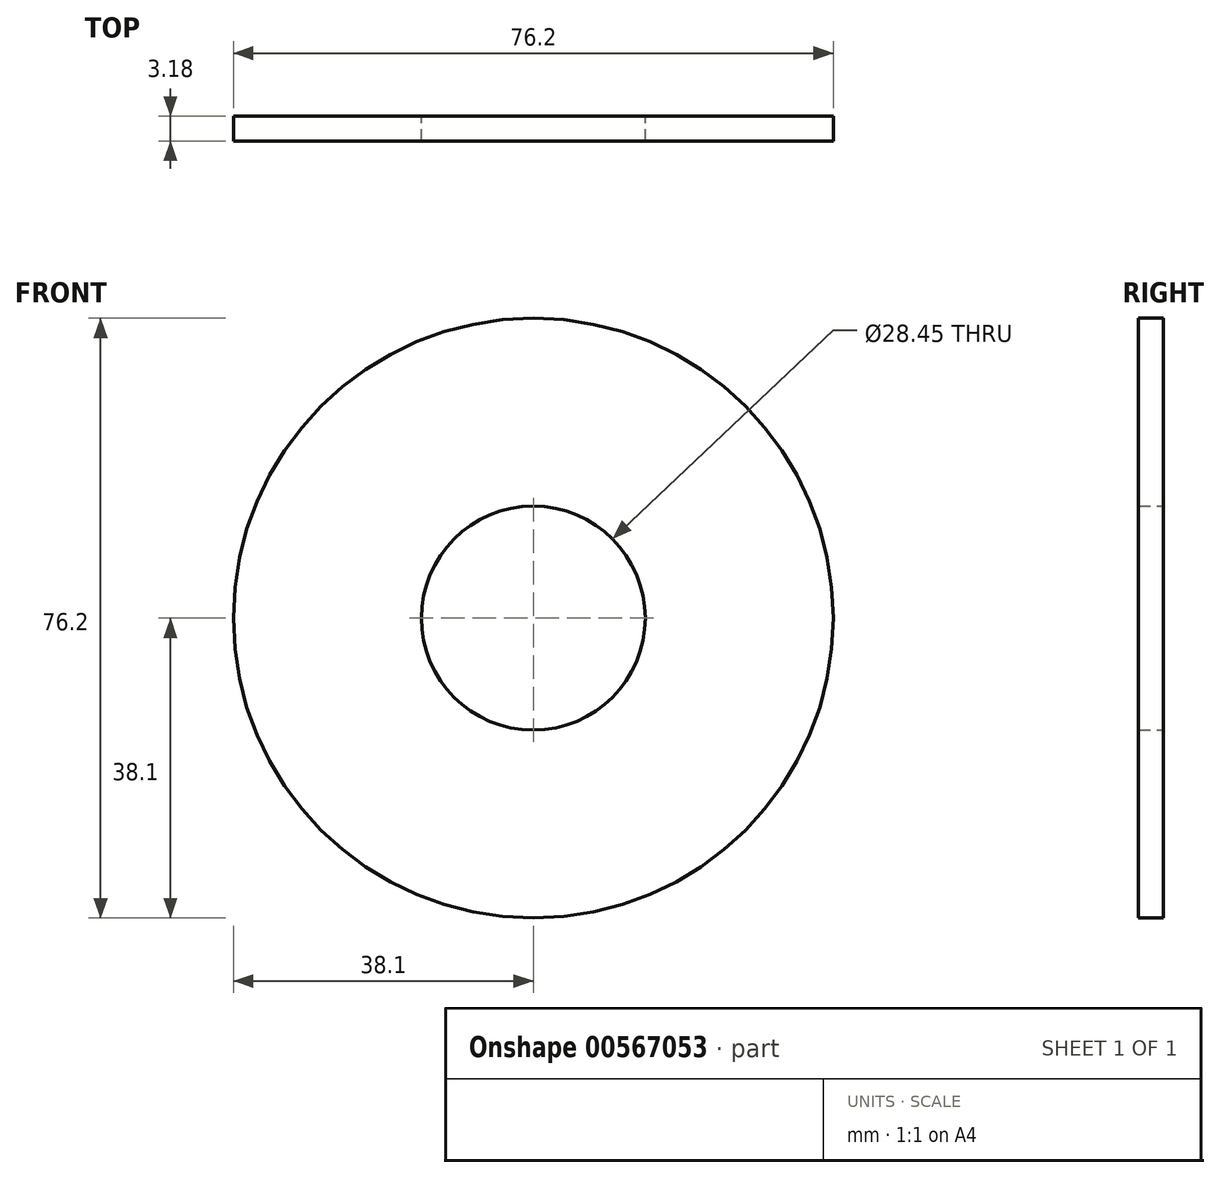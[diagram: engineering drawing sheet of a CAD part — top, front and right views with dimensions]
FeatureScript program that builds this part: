
annotation { "Feature Type Name" : "Feature", "Feature Type Description" : "" }
export const myFeature = defineFeature(function(context is Context, id is Id, definition is map)
    precondition{}
    {
        {
            var Q0;
            Q0=qCreatedBy(makeId("Front.planeOp"),FACE);
            var sketch = newSketch(context, id + "F0", { "sketchPlane" : qUnion([Q0])});
            skLineSegment(sketch, "E0.4", {"start": v(0, 0) * mm, "end": v(0, 0) * mm});
            skCircle(sketch, "E1", {"center": v(0, 0) * mm, "radius": 38.1 * mm});
            skCircle(sketch, "E2", {"center": v(0, 0) * mm, "radius": 14.22 * mm});
            skSolve(sketch);
        }
        {
            var Q0;
            Q0=qSketchRegion(id+"F0",true);
            extrude(context, id + "F1", {"entities" : qUnion([Q0]), "depth" : 3.17 * mm, "offsetDistance" : 25.4 * mm});
        }
    });
